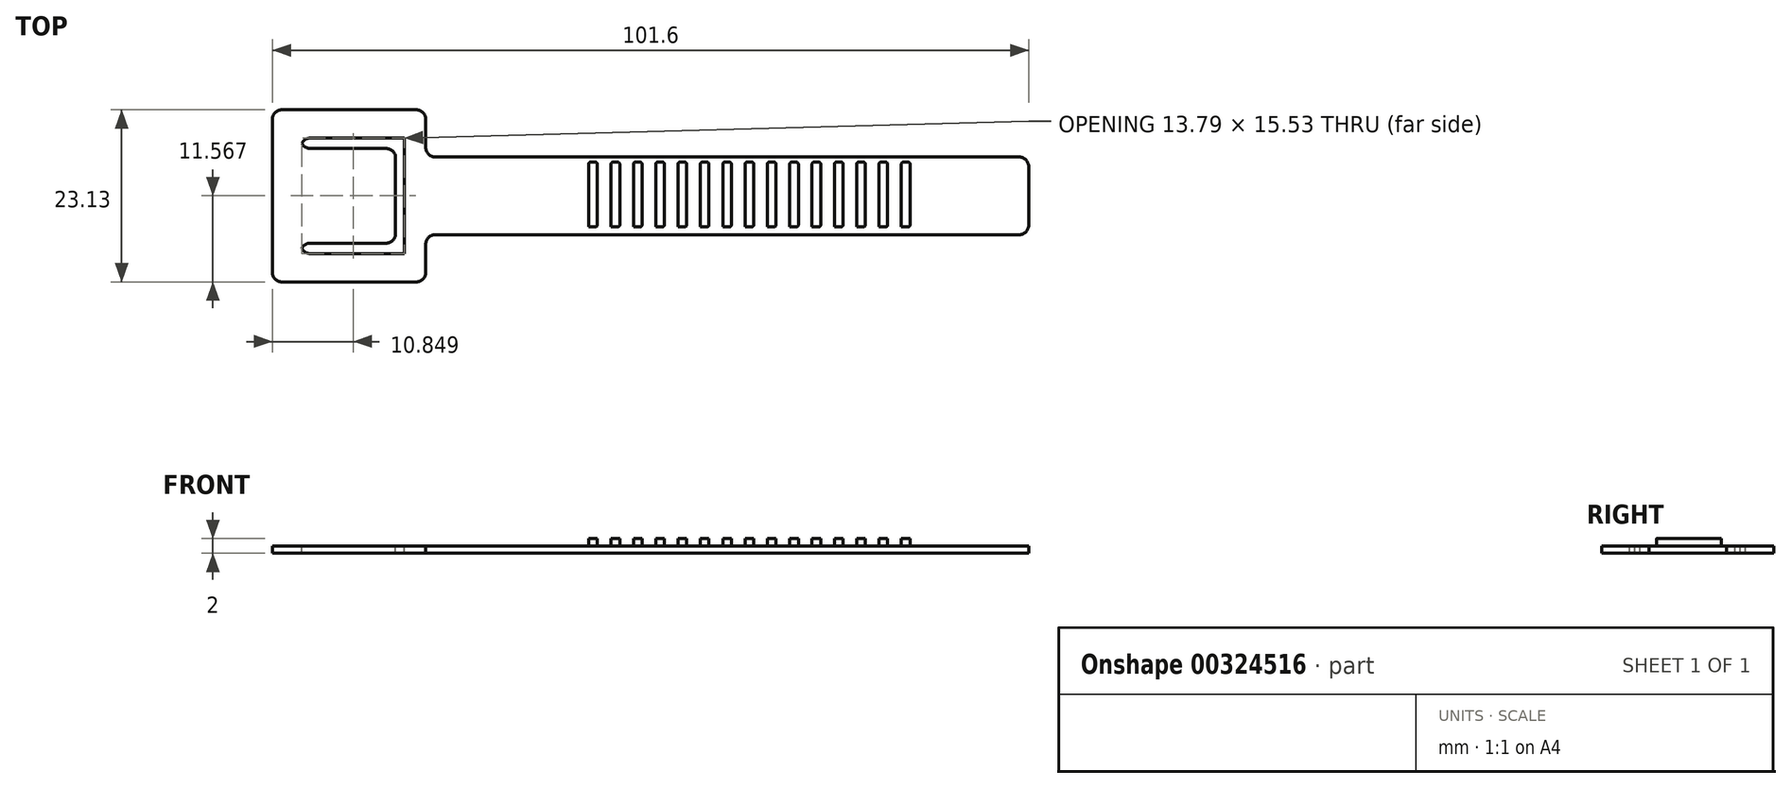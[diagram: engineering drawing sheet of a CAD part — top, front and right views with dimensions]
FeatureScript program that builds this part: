
annotation { "Feature Type Name" : "Feature", "Feature Type Description" : "" }
export const myFeature = defineFeature(function(context is Context, id is Id, definition is map)
    precondition{}
    {
        {
            var Q0;
            Q0=qCreatedBy(makeId("Top.planeOp"),FACE);
            var sketch = newSketch(context, id + "F0", { "sketchPlane" : qUnion([Q0])});
            skLineSegment(sketch, "E0.bottom", {"start": v(-20.62, 27.91) * mm, "end": v(57.84, 27.91) * mm});
            skLineSegment(sketch, "E0.top", {"start": v(-20.62, 17.48) * mm, "end": v(57.84, 17.48) * mm});
            skLineSegment(sketch, "E0.right", {"start": v(59.11, 26.64) * mm, "end": v(59.11, 18.75) * mm});
            skLineSegment(sketch, "E1.bottom", {"start": v(-23.16, 11.13) * mm, "end": v(-41.22, 11.13) * mm});
            skLineSegment(sketch, "E1.top", {"start": v(-23.16, 34.26) * mm, "end": v(-41.22, 34.26) * mm});
            skLineSegment(sketch, "E1.right", {"start": v(-42.49, 12.4) * mm, "end": v(-42.49, 33) * mm});
            skLineSegment(sketch, "E2", {"start": v(-21.9, 29.18) * mm, "end": v(-21.9, 33) * mm});
            skLineSegment(sketch, "E3", {"start": v(-21.9, 12.4) * mm, "end": v(-21.9, 16.21) * mm});
            skLineSegment(sketch, "E4.bottom", {"start": v(-38.17, 30.7) * mm, "end": v(-25.52, 30.7) * mm});
            skLineSegment(sketch, "E4.top", {"start": v(-38.17, 14.7) * mm, "end": v(-25.52, 14.7) * mm});
            skLineSegment(sketch, "E4.right", {"start": v(-25.52, 30.7) * mm, "end": v(-25.52, 14.7) * mm});
            skLineSegment(sketch, "E5", {"start": v(-39.44, 30.57) * mm, "end": v(-39.44, 29.43) * mm});
            skLineSegment(sketch, "E6", {"start": v(-38.17, 29.3) * mm, "end": v(-27.99, 29.3) * mm});
            skLineSegment(sketch, "E7", {"start": v(-26.72, 28.03) * mm, "end": v(-26.72, 17.36) * mm});
            skLineSegment(sketch, "E8", {"start": v(-27.99, 16.1) * mm, "end": v(-38.17, 16.1) * mm});
            skLineSegment(sketch, "E9", {"start": v(-39.44, 15.96) * mm, "end": v(-39.44, 14.82) * mm});
            skPoint(sketch, "E10.visualSharp", {"position": v(-26.72, 29.3) * mm});
            skArc(sketch, "E10.filletArc", {"start": v(-26.72, 28.03) * mm, "mid": v(-27.09, 28.93) * mm, "end": v(-27.99, 29.3) * mm});
            skPoint(sketch, "E11.visualSharp", {"position": v(-26.72, 16.1) * mm});
            skArc(sketch, "E11.filletArc", {"start": v(-27.99, 16.1) * mm, "mid": v(-27.09, 16.47) * mm, "end": v(-26.72, 17.36) * mm});
            skPoint(sketch, "E12.visualSharp", {"position": v(-39.44, 29.3) * mm});
            skArc(sketch, "E12.filletArc", {"start": v(-39.44, 30.57) * mm, "mid": v(-39.07, 29.67) * mm, "end": v(-38.17, 29.3) * mm});
            skPoint(sketch, "E13.visualSharp", {"position": v(-39.44, 30.7) * mm});
            skArc(sketch, "E13.filletArc", {"start": v(-38.17, 30.7) * mm, "mid": v(-39.07, 30.33) * mm, "end": v(-39.44, 29.43) * mm});
            skPoint(sketch, "E14.visualSharp", {"position": v(-39.44, 16.1) * mm});
            skArc(sketch, "E14.filletArc", {"start": v(-38.17, 16.1) * mm, "mid": v(-39.07, 15.72) * mm, "end": v(-39.44, 14.82) * mm});
            skPoint(sketch, "E15.visualSharp", {"position": v(-39.44, 14.7) * mm});
            skArc(sketch, "E15.filletArc", {"start": v(-39.44, 15.96) * mm, "mid": v(-39.07, 15.07) * mm, "end": v(-38.17, 14.7) * mm});
            skPoint(sketch, "E16.visualSharp", {"position": v(-21.9, 27.91) * mm});
            skArc(sketch, "E16.filletArc", {"start": v(-21.9, 29.18) * mm, "mid": v(-21.52, 28.29) * mm, "end": v(-20.62, 27.91) * mm});
            skPoint(sketch, "E17.visualSharp", {"position": v(-21.9, 17.48) * mm});
            skArc(sketch, "E17.filletArc", {"start": v(-20.62, 17.48) * mm, "mid": v(-21.52, 17.1) * mm, "end": v(-21.9, 16.21) * mm});
            skPoint(sketch, "E18.visualSharp", {"position": v(-21.9, 11.13) * mm});
            skArc(sketch, "E18.filletArc", {"start": v(-23.16, 11.13) * mm, "mid": v(-22.26, 11.5) * mm, "end": v(-21.9, 12.4) * mm});
            skPoint(sketch, "E19.visualSharp", {"position": v(-42.49, 11.13) * mm});
            skArc(sketch, "E19.filletArc", {"start": v(-42.49, 12.4) * mm, "mid": v(-42.12, 11.5) * mm, "end": v(-41.22, 11.13) * mm});
            skPoint(sketch, "E20.visualSharp", {"position": v(-42.49, 34.26) * mm});
            skArc(sketch, "E20.filletArc", {"start": v(-41.22, 34.26) * mm, "mid": v(-42.12, 33.9) * mm, "end": v(-42.49, 33) * mm});
            skPoint(sketch, "E21.visualSharp", {"position": v(-21.9, 34.26) * mm});
            skArc(sketch, "E21.filletArc", {"start": v(-21.9, 33) * mm, "mid": v(-22.26, 33.9) * mm, "end": v(-23.16, 34.26) * mm});
            skPoint(sketch, "E22.visualSharp", {"position": v(59.11, 27.91) * mm});
            skArc(sketch, "E22.filletArc", {"start": v(59.11, 26.64) * mm, "mid": v(58.74, 27.54) * mm, "end": v(57.84, 27.91) * mm});
            skPoint(sketch, "E23.visualSharp", {"position": v(59.11, 17.48) * mm});
            skArc(sketch, "E23.filletArc", {"start": v(57.84, 17.48) * mm, "mid": v(58.74, 17.85) * mm, "end": v(59.11, 18.75) * mm});
            skSolve(sketch);
        }
        {
            var Q0;
            Q0=makeQuery(id+"F0.imprint","IMPRINT",FACE,{"disambiguationData":[TD([[makeQuery(id+"F0.imprint","IMPRINT",EDGE,{"derivedFrom":sQuery(id+"F0.wireOp",EDGE,"E0.bottom")}),-1.0]])]});
            var Q1;
            {var subQ5=sQuery(id+"F0.wireOp",EDGE,"E4.bottom");Q1=makeQuery(id+"F0.imprint","IMPRINT",FACE,{"disambiguationData":[TD([[makeQuery(id+"F0.imprint","IMPRINT",EDGE,{"derivedFrom":subQ5}),-1.0]])]});}
            var Q2;
            {var subQ0=sQuery(id+"F0.wireOp",EDGE,"E5");Q2=makeQuery(id+"F0.imprint","IMPRINT",FACE,{"disambiguationData":[TD([[makeQuery(id+"F0.imprint","IMPRINT",EDGE,{"derivedFrom":subQ0}),1.0]])]});}
            var Q3;
            {var subQ0=sQuery(id+"F0.wireOp",EDGE,"E9");Q3=makeQuery(id+"F0.imprint","IMPRINT",FACE,{"disambiguationData":[TD([[makeQuery(id+"F0.imprint","IMPRINT",EDGE,{"derivedFrom":subQ0}),1.0]])]});}
            extrude(context, id + "F1", {"entities" : qUnion([Q0, Q1, Q2, Q3]), "depth" : 1 * mm});
        }
        {
            var Q0;
            Q0=makeQuery(id+"F1.opExtrude","CAP_FACE",FACE,{"disambiguationData":[OSD([sQuery(id+"F0.wireOp",EDGE,"E0.bottom"),sQuery(id+"F0.wireOp",EDGE,"E0.top"),sQuery(id+"F0.wireOp",EDGE,"E0.right"),sQuery(id+"F0.wireOp",EDGE,"E1.bottom"),sQuery(id+"F0.wireOp",EDGE,"E1.top"),sQuery(id+"F0.wireOp",EDGE,"E1.right"),sQuery(id+"F0.wireOp",EDGE,"E2"),sQuery(id+"F0.wireOp",EDGE,"E3"),sQuery(id+"F0.wireOp",EDGE,"E16.filletArc"),sQuery(id+"F0.wireOp",EDGE,"E17.filletArc"),sQuery(id+"F0.wireOp",EDGE,"E18.filletArc"),sQuery(id+"F0.wireOp",EDGE,"E19.filletArc"),sQuery(id+"F0.wireOp",EDGE,"E20.filletArc"),sQuery(id+"F0.wireOp",EDGE,"E21.filletArc"),sQuery(id+"F0.wireOp",EDGE,"E22.filletArc"),sQuery(id+"F0.wireOp",EDGE,"E23.filletArc")])],"isStart":false});
            var sketch = newSketch(context, id + "F2", { "sketchPlane" : qUnion([Q0])});
            skLineSegment(sketch, "E24.bottom", {"start": v(-37.4, 30.46) * mm, "end": v(-24.74, 30.46) * mm});
            skLineSegment(sketch, "E24.top", {"start": v(-37.4, 14.93) * mm, "end": v(-24.74, 14.93) * mm});
            skLineSegment(sketch, "E24.right", {"start": v(-24.74, 30.46) * mm, "end": v(-24.74, 14.93) * mm});
            skLineSegment(sketch, "E25", {"start": v(-37.4, 29.06) * mm, "end": v(-27.21, 29.06) * mm});
            skLineSegment(sketch, "E26", {"start": v(-25.94, 27.8) * mm, "end": v(-25.94, 17.6) * mm});
            skLineSegment(sketch, "E27", {"start": v(-27.21, 16.33) * mm, "end": v(-37.4, 16.33) * mm});
            skPoint(sketch, "E28.visualSharp", {"position": v(-25.94, 29.06) * mm});
            skArc(sketch, "E28.filletArc", {"start": v(-25.94, 27.8) * mm, "mid": v(-26.32, 28.7) * mm, "end": v(-27.21, 29.06) * mm});
            skPoint(sketch, "E29.visualSharp", {"position": v(-25.94, 16.33) * mm});
            skArc(sketch, "E29.filletArc", {"start": v(-27.21, 16.33) * mm, "mid": v(-26.32, 16.7) * mm, "end": v(-25.94, 17.6) * mm});
            skPoint(sketch, "E30.visualSharp", {"position": v(-38.67, 29.06) * mm});
            skArc(sketch, "E30.filletArc", {"start": v(-38.67, 30.33) * mm, "mid": v(-38.3, 29.43) * mm, "end": v(-37.4, 29.06) * mm});
            skPoint(sketch, "E31.visualSharp", {"position": v(-38.67, 30.46) * mm});
            skArc(sketch, "E31.filletArc", {"start": v(-37.4, 30.46) * mm, "mid": v(-38.3, 30.1) * mm, "end": v(-38.67, 29.2) * mm});
            skPoint(sketch, "E32.visualSharp", {"position": v(-38.67, 16.33) * mm});
            skArc(sketch, "E32.filletArc", {"start": v(-37.4, 16.33) * mm, "mid": v(-38.3, 15.96) * mm, "end": v(-38.67, 15.06) * mm});
            skPoint(sketch, "E33.visualSharp", {"position": v(-38.67, 14.93) * mm});
            skArc(sketch, "E33.filletArc", {"start": v(-38.67, 16.2) * mm, "mid": v(-38.3, 15.3) * mm, "end": v(-37.4, 14.93) * mm});
            skLineSegment(sketch, "E34", {"start": v(-32.3, 30.46) * mm, "end": v(-32.3, 34.26) * mm});
            skLineSegment(sketch, "E35", {"start": v(-32.19, 11.13) * mm, "end": v(-32.19, 14.93) * mm});
            skSolve(sketch);
        }
        {
            var Q0;
            Q0 = qSketchRegion(id + "F2", true);
            extrude(context, id + "F3", {"entities" : qUnion([Q0]), "operationType" : NewBodyOperationType.REMOVE, "oppositeDirection" : true, "depth" : 25.4 * mm});
        }
        {
            var Q0;
            Q0=makeQuery(id+"F1.opExtrude","CAP_FACE",FACE,{"disambiguationData":[OSD([sQuery(id+"F0.wireOp",EDGE,"E0.bottom"),sQuery(id+"F0.wireOp",EDGE,"E0.top"),sQuery(id+"F0.wireOp",EDGE,"E0.right"),sQuery(id+"F0.wireOp",EDGE,"E1.bottom"),sQuery(id+"F0.wireOp",EDGE,"E1.top"),sQuery(id+"F0.wireOp",EDGE,"E1.right"),sQuery(id+"F0.wireOp",EDGE,"E2"),sQuery(id+"F0.wireOp",EDGE,"E3"),sQuery(id+"F0.wireOp",EDGE,"E16.filletArc"),sQuery(id+"F0.wireOp",EDGE,"E17.filletArc"),sQuery(id+"F0.wireOp",EDGE,"E18.filletArc"),sQuery(id+"F0.wireOp",EDGE,"E19.filletArc"),sQuery(id+"F0.wireOp",EDGE,"E20.filletArc"),sQuery(id+"F0.wireOp",EDGE,"E21.filletArc"),sQuery(id+"F0.wireOp",EDGE,"E22.filletArc"),sQuery(id+"F0.wireOp",EDGE,"E23.filletArc")])],"isStart":false});
            var sketch = newSketch(context, id + "F4", { "sketchPlane" : qUnion([Q0])});
            skLineSegment(sketch, "E36.bottom", {"start": v(0.25, 27.22) * mm, "end": v(0.9, 27.22) * mm});
            skLineSegment(sketch, "E36.left", {"start": v(0, 26.97) * mm, "end": v(0, 18.42) * mm});
            skArc(sketch, "E37.filletArc", {"start": v(1.16, 26.97) * mm, "mid": v(1.09, 27.15) * mm, "end": v(0.9, 27.22) * mm});
            skPoint(sketch, "E38.visualSharp", {"position": v(0, 27.22) * mm});
            skArc(sketch, "E38.filletArc", {"start": v(0.25, 27.22) * mm, "mid": v(0.07, 27.15) * mm, "end": v(0, 26.97) * mm});
            skPoint(sketch, "E39.visualSharp", {"position": v(0, 18.51) * mm});
            skArc(sketch, "E39.filletArc", {"start": v(0, 18.42) * mm, "mid": v(-0.15, 18.36) * mm, "end": v(-0.09, 18.51) * mm});
            skLineSegment(sketch, "E40", {"start": v(1.16, 26.97) * mm, "end": v(1.16, 18.78) * mm});
            skLineSegment(sketch, "E41", {"start": v(0.91, 18.53) * mm, "end": v(0, 18.51) * mm});
            skPoint(sketch, "E42.visualSharp", {"position": v(1.16, 18.53) * mm});
            skArc(sketch, "E42.filletArc", {"start": v(0.91, 18.53) * mm, "mid": v(1.09, 18.6) * mm, "end": v(1.16, 18.78) * mm});
            skPoint(sketch, "E43.1.0.0", {"position": v(4.16, 18.53) * mm});
            skPoint(sketch, "E43.1.0.1", {"position": v(3, 18.51) * mm});
            skLineSegment(sketch, "E43.1.0.2", {"start": v(3.25, 27.22) * mm, "end": v(3.9, 27.22) * mm});
            skLineSegment(sketch, "E43.1.0.3", {"start": v(3, 26.97) * mm, "end": v(3, 18.42) * mm});
            skPoint(sketch, "E43.1.0.4", {"position": v(3, 27.22) * mm});
            skLineSegment(sketch, "E43.1.0.5", {"start": v(4.16, 26.97) * mm, "end": v(4.16, 18.78) * mm});
            skLineSegment(sketch, "E43.1.0.6", {"start": v(3.91, 18.53) * mm, "end": v(3, 18.51) * mm});
            skArc(sketch, "E43.1.0.7", {"start": v(4.16, 26.97) * mm, "mid": v(4.09, 27.15) * mm, "end": v(3.9, 27.22) * mm});
            skArc(sketch, "E43.1.0.8", {"start": v(3.25, 27.22) * mm, "mid": v(3.07, 27.15) * mm, "end": v(3, 26.97) * mm});
            skArc(sketch, "E43.1.0.9", {"start": v(3, 18.42) * mm, "mid": v(2.85, 18.36) * mm, "end": v(2.91, 18.51) * mm});
            skArc(sketch, "E43.1.0.10", {"start": v(3.91, 18.53) * mm, "mid": v(4.09, 18.6) * mm, "end": v(4.16, 18.78) * mm});
            skPoint(sketch, "E43.2.0.0", {"position": v(7.16, 18.53) * mm});
            skPoint(sketch, "E43.2.0.1", {"position": v(6, 18.51) * mm});
            skLineSegment(sketch, "E43.2.0.2", {"start": v(6.25, 27.22) * mm, "end": v(6.9, 27.22) * mm});
            skLineSegment(sketch, "E43.2.0.3", {"start": v(6, 26.97) * mm, "end": v(6, 18.42) * mm});
            skPoint(sketch, "E43.2.0.4", {"position": v(6, 27.22) * mm});
            skLineSegment(sketch, "E43.2.0.5", {"start": v(7.16, 26.97) * mm, "end": v(7.16, 18.78) * mm});
            skLineSegment(sketch, "E43.2.0.6", {"start": v(6.91, 18.53) * mm, "end": v(6, 18.51) * mm});
            skArc(sketch, "E43.2.0.7", {"start": v(7.16, 26.97) * mm, "mid": v(7.09, 27.15) * mm, "end": v(6.9, 27.22) * mm});
            skArc(sketch, "E43.2.0.8", {"start": v(6.25, 27.22) * mm, "mid": v(6.07, 27.15) * mm, "end": v(6, 26.97) * mm});
            skArc(sketch, "E43.2.0.9", {"start": v(6, 18.42) * mm, "mid": v(5.85, 18.36) * mm, "end": v(5.91, 18.51) * mm});
            skArc(sketch, "E43.2.0.10", {"start": v(6.91, 18.53) * mm, "mid": v(7.09, 18.6) * mm, "end": v(7.16, 18.78) * mm});
            skPoint(sketch, "E43.3.0.0", {"position": v(10.16, 18.53) * mm});
            skPoint(sketch, "E43.3.0.1", {"position": v(9, 18.51) * mm});
            skLineSegment(sketch, "E43.3.0.2", {"start": v(9.25, 27.22) * mm, "end": v(9.9, 27.22) * mm});
            skLineSegment(sketch, "E43.3.0.3", {"start": v(9, 26.97) * mm, "end": v(9, 18.42) * mm});
            skPoint(sketch, "E43.3.0.4", {"position": v(9, 27.22) * mm});
            skLineSegment(sketch, "E43.3.0.5", {"start": v(10.16, 26.97) * mm, "end": v(10.16, 18.78) * mm});
            skLineSegment(sketch, "E43.3.0.6", {"start": v(9.91, 18.53) * mm, "end": v(9, 18.51) * mm});
            skArc(sketch, "E43.3.0.7", {"start": v(10.16, 26.97) * mm, "mid": v(10.09, 27.15) * mm, "end": v(9.9, 27.22) * mm});
            skArc(sketch, "E43.3.0.8", {"start": v(9.25, 27.22) * mm, "mid": v(9.07, 27.15) * mm, "end": v(9, 26.97) * mm});
            skArc(sketch, "E43.3.0.9", {"start": v(9, 18.42) * mm, "mid": v(8.85, 18.36) * mm, "end": v(8.91, 18.51) * mm});
            skArc(sketch, "E43.3.0.10", {"start": v(9.91, 18.53) * mm, "mid": v(10.09, 18.6) * mm, "end": v(10.16, 18.78) * mm});
            skPoint(sketch, "E43.4.0.0", {"position": v(13.16, 18.53) * mm});
            skPoint(sketch, "E43.4.0.1", {"position": v(12, 18.51) * mm});
            skLineSegment(sketch, "E43.4.0.2", {"start": v(12.25, 27.22) * mm, "end": v(12.9, 27.22) * mm});
            skLineSegment(sketch, "E43.4.0.3", {"start": v(12, 26.97) * mm, "end": v(12, 18.42) * mm});
            skPoint(sketch, "E43.4.0.4", {"position": v(12, 27.22) * mm});
            skLineSegment(sketch, "E43.4.0.5", {"start": v(13.16, 26.97) * mm, "end": v(13.16, 18.78) * mm});
            skLineSegment(sketch, "E43.4.0.6", {"start": v(12.91, 18.53) * mm, "end": v(12, 18.51) * mm});
            skArc(sketch, "E43.4.0.7", {"start": v(13.16, 26.97) * mm, "mid": v(13.09, 27.15) * mm, "end": v(12.9, 27.22) * mm});
            skArc(sketch, "E43.4.0.8", {"start": v(12.25, 27.22) * mm, "mid": v(12.07, 27.15) * mm, "end": v(12, 26.97) * mm});
            skArc(sketch, "E43.4.0.9", {"start": v(12, 18.42) * mm, "mid": v(11.85, 18.36) * mm, "end": v(11.91, 18.51) * mm});
            skArc(sketch, "E43.4.0.10", {"start": v(12.91, 18.53) * mm, "mid": v(13.09, 18.6) * mm, "end": v(13.16, 18.78) * mm});
            skPoint(sketch, "E43.5.0.0", {"position": v(16.16, 18.53) * mm});
            skPoint(sketch, "E43.5.0.1", {"position": v(15, 18.51) * mm});
            skLineSegment(sketch, "E43.5.0.2", {"start": v(15.25, 27.22) * mm, "end": v(15.9, 27.22) * mm});
            skLineSegment(sketch, "E43.5.0.3", {"start": v(15, 26.97) * mm, "end": v(15, 18.42) * mm});
            skPoint(sketch, "E43.5.0.4", {"position": v(15, 27.22) * mm});
            skLineSegment(sketch, "E43.5.0.5", {"start": v(16.16, 26.97) * mm, "end": v(16.16, 18.78) * mm});
            skLineSegment(sketch, "E43.5.0.6", {"start": v(15.91, 18.53) * mm, "end": v(15, 18.51) * mm});
            skArc(sketch, "E43.5.0.7", {"start": v(16.16, 26.97) * mm, "mid": v(16.09, 27.15) * mm, "end": v(15.9, 27.22) * mm});
            skArc(sketch, "E43.5.0.8", {"start": v(15.25, 27.22) * mm, "mid": v(15.07, 27.15) * mm, "end": v(15, 26.97) * mm});
            skArc(sketch, "E43.5.0.9", {"start": v(15, 18.42) * mm, "mid": v(14.85, 18.36) * mm, "end": v(14.91, 18.51) * mm});
            skArc(sketch, "E43.5.0.10", {"start": v(15.91, 18.53) * mm, "mid": v(16.09, 18.6) * mm, "end": v(16.16, 18.78) * mm});
            skPoint(sketch, "E43.6.0.0", {"position": v(19.16, 18.53) * mm});
            skPoint(sketch, "E43.6.0.1", {"position": v(18, 18.51) * mm});
            skLineSegment(sketch, "E43.6.0.2", {"start": v(18.25, 27.22) * mm, "end": v(18.9, 27.22) * mm});
            skLineSegment(sketch, "E43.6.0.3", {"start": v(18, 26.97) * mm, "end": v(18, 18.42) * mm});
            skPoint(sketch, "E43.6.0.4", {"position": v(18, 27.22) * mm});
            skLineSegment(sketch, "E43.6.0.5", {"start": v(19.16, 26.97) * mm, "end": v(19.16, 18.78) * mm});
            skLineSegment(sketch, "E43.6.0.6", {"start": v(18.91, 18.53) * mm, "end": v(18, 18.51) * mm});
            skArc(sketch, "E43.6.0.7", {"start": v(19.16, 26.97) * mm, "mid": v(19.09, 27.15) * mm, "end": v(18.9, 27.22) * mm});
            skArc(sketch, "E43.6.0.8", {"start": v(18.25, 27.22) * mm, "mid": v(18.07, 27.15) * mm, "end": v(18, 26.97) * mm});
            skArc(sketch, "E43.6.0.9", {"start": v(18, 18.42) * mm, "mid": v(17.85, 18.36) * mm, "end": v(17.91, 18.51) * mm});
            skArc(sketch, "E43.6.0.10", {"start": v(18.91, 18.53) * mm, "mid": v(19.09, 18.6) * mm, "end": v(19.16, 18.78) * mm});
            skPoint(sketch, "E43.7.0.0", {"position": v(22.16, 18.53) * mm});
            skPoint(sketch, "E43.7.0.1", {"position": v(21, 18.51) * mm});
            skLineSegment(sketch, "E43.7.0.2", {"start": v(21.25, 27.22) * mm, "end": v(21.9, 27.22) * mm});
            skLineSegment(sketch, "E43.7.0.3", {"start": v(21, 26.97) * mm, "end": v(21, 18.42) * mm});
            skPoint(sketch, "E43.7.0.4", {"position": v(21, 27.22) * mm});
            skLineSegment(sketch, "E43.7.0.5", {"start": v(22.16, 26.97) * mm, "end": v(22.16, 18.78) * mm});
            skLineSegment(sketch, "E43.7.0.6", {"start": v(21.91, 18.53) * mm, "end": v(21, 18.51) * mm});
            skArc(sketch, "E43.7.0.7", {"start": v(22.16, 26.97) * mm, "mid": v(22.09, 27.15) * mm, "end": v(21.9, 27.22) * mm});
            skArc(sketch, "E43.7.0.8", {"start": v(21.25, 27.22) * mm, "mid": v(21.07, 27.15) * mm, "end": v(21, 26.97) * mm});
            skArc(sketch, "E43.7.0.9", {"start": v(21, 18.42) * mm, "mid": v(20.85, 18.36) * mm, "end": v(20.91, 18.51) * mm});
            skArc(sketch, "E43.7.0.10", {"start": v(21.91, 18.53) * mm, "mid": v(22.09, 18.6) * mm, "end": v(22.16, 18.78) * mm});
            skPoint(sketch, "E43.8.0.0", {"position": v(25.16, 18.53) * mm});
            skPoint(sketch, "E43.8.0.1", {"position": v(24, 18.51) * mm});
            skLineSegment(sketch, "E43.8.0.2", {"start": v(24.25, 27.22) * mm, "end": v(24.9, 27.22) * mm});
            skLineSegment(sketch, "E43.8.0.3", {"start": v(24, 26.97) * mm, "end": v(24, 18.42) * mm});
            skPoint(sketch, "E43.8.0.4", {"position": v(24, 27.22) * mm});
            skLineSegment(sketch, "E43.8.0.5", {"start": v(25.16, 26.97) * mm, "end": v(25.16, 18.78) * mm});
            skLineSegment(sketch, "E43.8.0.6", {"start": v(24.91, 18.53) * mm, "end": v(24, 18.51) * mm});
            skArc(sketch, "E43.8.0.7", {"start": v(25.16, 26.97) * mm, "mid": v(25.09, 27.15) * mm, "end": v(24.9, 27.22) * mm});
            skArc(sketch, "E43.8.0.8", {"start": v(24.25, 27.22) * mm, "mid": v(24.07, 27.15) * mm, "end": v(24, 26.97) * mm});
            skArc(sketch, "E43.8.0.9", {"start": v(24, 18.42) * mm, "mid": v(23.85, 18.36) * mm, "end": v(23.91, 18.51) * mm});
            skArc(sketch, "E43.8.0.10", {"start": v(24.91, 18.53) * mm, "mid": v(25.09, 18.6) * mm, "end": v(25.16, 18.78) * mm});
            skPoint(sketch, "E43.9.0.0", {"position": v(28.16, 18.53) * mm});
            skPoint(sketch, "E43.9.0.1", {"position": v(27, 18.51) * mm});
            skLineSegment(sketch, "E43.9.0.2", {"start": v(27.25, 27.22) * mm, "end": v(27.9, 27.22) * mm});
            skLineSegment(sketch, "E43.9.0.3", {"start": v(27, 26.97) * mm, "end": v(27, 18.42) * mm});
            skPoint(sketch, "E43.9.0.4", {"position": v(27, 27.22) * mm});
            skLineSegment(sketch, "E43.9.0.5", {"start": v(28.16, 26.97) * mm, "end": v(28.16, 18.78) * mm});
            skLineSegment(sketch, "E43.9.0.6", {"start": v(27.91, 18.53) * mm, "end": v(27, 18.51) * mm});
            skArc(sketch, "E43.9.0.7", {"start": v(28.16, 26.97) * mm, "mid": v(28.09, 27.15) * mm, "end": v(27.9, 27.22) * mm});
            skArc(sketch, "E43.9.0.8", {"start": v(27.25, 27.22) * mm, "mid": v(27.07, 27.15) * mm, "end": v(27, 26.97) * mm});
            skArc(sketch, "E43.9.0.9", {"start": v(27, 18.42) * mm, "mid": v(26.85, 18.36) * mm, "end": v(26.91, 18.51) * mm});
            skArc(sketch, "E43.9.0.10", {"start": v(27.91, 18.53) * mm, "mid": v(28.09, 18.6) * mm, "end": v(28.16, 18.78) * mm});
            skPoint(sketch, "E43.10.0.0", {"position": v(31.16, 18.53) * mm});
            skPoint(sketch, "E43.10.0.1", {"position": v(30, 18.51) * mm});
            skLineSegment(sketch, "E43.10.0.2", {"start": v(30.25, 27.22) * mm, "end": v(30.9, 27.22) * mm});
            skLineSegment(sketch, "E43.10.0.3", {"start": v(30, 26.97) * mm, "end": v(30, 18.42) * mm});
            skPoint(sketch, "E43.10.0.4", {"position": v(30, 27.22) * mm});
            skLineSegment(sketch, "E43.10.0.5", {"start": v(31.16, 26.97) * mm, "end": v(31.16, 18.78) * mm});
            skLineSegment(sketch, "E43.10.0.6", {"start": v(30.91, 18.53) * mm, "end": v(30, 18.51) * mm});
            skArc(sketch, "E43.10.0.7", {"start": v(31.16, 26.97) * mm, "mid": v(31.09, 27.15) * mm, "end": v(30.9, 27.22) * mm});
            skArc(sketch, "E43.10.0.8", {"start": v(30.25, 27.22) * mm, "mid": v(30.07, 27.15) * mm, "end": v(30, 26.97) * mm});
            skArc(sketch, "E43.10.0.9", {"start": v(30, 18.42) * mm, "mid": v(29.85, 18.36) * mm, "end": v(29.91, 18.51) * mm});
            skArc(sketch, "E43.10.0.10", {"start": v(30.91, 18.53) * mm, "mid": v(31.09, 18.6) * mm, "end": v(31.16, 18.78) * mm});
            skPoint(sketch, "E43.11.0.0", {"position": v(34.16, 18.53) * mm});
            skPoint(sketch, "E43.11.0.1", {"position": v(33, 18.51) * mm});
            skLineSegment(sketch, "E43.11.0.2", {"start": v(33.25, 27.22) * mm, "end": v(33.9, 27.22) * mm});
            skLineSegment(sketch, "E43.11.0.3", {"start": v(33, 26.97) * mm, "end": v(33, 18.42) * mm});
            skPoint(sketch, "E43.11.0.4", {"position": v(33, 27.22) * mm});
            skLineSegment(sketch, "E43.11.0.5", {"start": v(34.16, 26.97) * mm, "end": v(34.16, 18.78) * mm});
            skLineSegment(sketch, "E43.11.0.6", {"start": v(33.91, 18.53) * mm, "end": v(33, 18.51) * mm});
            skArc(sketch, "E43.11.0.7", {"start": v(34.16, 26.97) * mm, "mid": v(34.09, 27.15) * mm, "end": v(33.9, 27.22) * mm});
            skArc(sketch, "E43.11.0.8", {"start": v(33.25, 27.22) * mm, "mid": v(33.07, 27.15) * mm, "end": v(33, 26.97) * mm});
            skArc(sketch, "E43.11.0.9", {"start": v(33, 18.42) * mm, "mid": v(32.85, 18.36) * mm, "end": v(32.91, 18.51) * mm});
            skArc(sketch, "E43.11.0.10", {"start": v(33.91, 18.53) * mm, "mid": v(34.09, 18.6) * mm, "end": v(34.16, 18.78) * mm});
            skPoint(sketch, "E43.12.0.0", {"position": v(37.16, 18.53) * mm});
            skPoint(sketch, "E43.12.0.1", {"position": v(36, 18.51) * mm});
            skLineSegment(sketch, "E43.12.0.2", {"start": v(36.25, 27.22) * mm, "end": v(36.9, 27.22) * mm});
            skLineSegment(sketch, "E43.12.0.3", {"start": v(36, 26.97) * mm, "end": v(36, 18.42) * mm});
            skPoint(sketch, "E43.12.0.4", {"position": v(36, 27.22) * mm});
            skLineSegment(sketch, "E43.12.0.5", {"start": v(37.16, 26.97) * mm, "end": v(37.16, 18.78) * mm});
            skLineSegment(sketch, "E43.12.0.6", {"start": v(36.91, 18.53) * mm, "end": v(36, 18.51) * mm});
            skArc(sketch, "E43.12.0.7", {"start": v(37.16, 26.97) * mm, "mid": v(37.09, 27.15) * mm, "end": v(36.9, 27.22) * mm});
            skArc(sketch, "E43.12.0.8", {"start": v(36.25, 27.22) * mm, "mid": v(36.07, 27.15) * mm, "end": v(36, 26.97) * mm});
            skArc(sketch, "E43.12.0.9", {"start": v(36, 18.42) * mm, "mid": v(35.85, 18.36) * mm, "end": v(35.91, 18.51) * mm});
            skArc(sketch, "E43.12.0.10", {"start": v(36.91, 18.53) * mm, "mid": v(37.09, 18.6) * mm, "end": v(37.16, 18.78) * mm});
            skPoint(sketch, "E43.13.0.0", {"position": v(40.16, 18.53) * mm});
            skPoint(sketch, "E43.13.0.1", {"position": v(39, 18.51) * mm});
            skLineSegment(sketch, "E43.13.0.2", {"start": v(39.25, 27.22) * mm, "end": v(39.9, 27.22) * mm});
            skLineSegment(sketch, "E43.13.0.3", {"start": v(39, 26.97) * mm, "end": v(39, 18.42) * mm});
            skPoint(sketch, "E43.13.0.4", {"position": v(39, 27.22) * mm});
            skLineSegment(sketch, "E43.13.0.5", {"start": v(40.16, 26.97) * mm, "end": v(40.16, 18.78) * mm});
            skLineSegment(sketch, "E43.13.0.6", {"start": v(39.91, 18.53) * mm, "end": v(39, 18.51) * mm});
            skArc(sketch, "E43.13.0.7", {"start": v(40.16, 26.97) * mm, "mid": v(40.09, 27.15) * mm, "end": v(39.9, 27.22) * mm});
            skArc(sketch, "E43.13.0.8", {"start": v(39.25, 27.22) * mm, "mid": v(39.07, 27.15) * mm, "end": v(39, 26.97) * mm});
            skArc(sketch, "E43.13.0.9", {"start": v(39, 18.42) * mm, "mid": v(38.85, 18.36) * mm, "end": v(38.91, 18.51) * mm});
            skArc(sketch, "E43.13.0.10", {"start": v(39.91, 18.53) * mm, "mid": v(40.09, 18.6) * mm, "end": v(40.16, 18.78) * mm});
            skPoint(sketch, "E43.14.0.0", {"position": v(43.16, 18.53) * mm});
            skPoint(sketch, "E43.14.0.1", {"position": v(42, 18.51) * mm});
            skLineSegment(sketch, "E43.14.0.2", {"start": v(42.25, 27.22) * mm, "end": v(42.9, 27.22) * mm});
            skLineSegment(sketch, "E43.14.0.3", {"start": v(42, 26.97) * mm, "end": v(42, 18.42) * mm});
            skPoint(sketch, "E43.14.0.4", {"position": v(42, 27.22) * mm});
            skLineSegment(sketch, "E43.14.0.5", {"start": v(43.16, 26.97) * mm, "end": v(43.16, 18.78) * mm});
            skLineSegment(sketch, "E43.14.0.6", {"start": v(42.91, 18.53) * mm, "end": v(42, 18.51) * mm});
            skArc(sketch, "E43.14.0.7", {"start": v(43.16, 26.97) * mm, "mid": v(43.09, 27.15) * mm, "end": v(42.9, 27.22) * mm});
            skArc(sketch, "E43.14.0.8", {"start": v(42.25, 27.22) * mm, "mid": v(42.07, 27.15) * mm, "end": v(42, 26.97) * mm});
            skArc(sketch, "E43.14.0.9", {"start": v(42, 18.42) * mm, "mid": v(41.85, 18.36) * mm, "end": v(41.91, 18.51) * mm});
            skArc(sketch, "E43.14.0.10", {"start": v(42.91, 18.53) * mm, "mid": v(43.09, 18.6) * mm, "end": v(43.16, 18.78) * mm});
            skLineSegment(sketch, "E43.direction1", {"start": v(-0.09, 18.42) * mm, "end": v(2.91, 18.42) * mm, "construction": true});
            skSolve(sketch);
        }
        {
            var Q0;
            Q0=makeQuery(id+"F4.imprint","IMPRINT",FACE,{"disambiguationData":[TD([[makeQuery(id+"F4.imprint","IMPRINT",EDGE,{"derivedFrom":sQuery(id+"F4.wireOp",EDGE,"E36.bottom")}),-1.0]])]});
            var Q1;
            Q1=makeQuery(id+"F4.imprint","IMPRINT",FACE,{"disambiguationData":[TD([[makeQuery(id+"F4.imprint","IMPRINT",EDGE,{"derivedFrom":sQuery(id+"F4.wireOp",EDGE,"E43.1.0.2")}),-1.0]])]});
            var Q2;
            Q2=makeQuery(id+"F4.imprint","IMPRINT",FACE,{"disambiguationData":[TD([[makeQuery(id+"F4.imprint","IMPRINT",EDGE,{"derivedFrom":sQuery(id+"F4.wireOp",EDGE,"E43.2.0.2")}),-1.0]])]});
            var Q3;
            Q3=makeQuery(id+"F4.imprint","IMPRINT",FACE,{"disambiguationData":[TD([[makeQuery(id+"F4.imprint","IMPRINT",EDGE,{"derivedFrom":sQuery(id+"F4.wireOp",EDGE,"E43.3.0.2")}),-1.0]])]});
            var Q4;
            Q4=makeQuery(id+"F4.imprint","IMPRINT",FACE,{"disambiguationData":[TD([[makeQuery(id+"F4.imprint","IMPRINT",EDGE,{"derivedFrom":sQuery(id+"F4.wireOp",EDGE,"E43.4.0.2")}),-1.0]])]});
            var Q5;
            Q5=makeQuery(id+"F4.imprint","IMPRINT",FACE,{"disambiguationData":[TD([[makeQuery(id+"F4.imprint","IMPRINT",EDGE,{"derivedFrom":sQuery(id+"F4.wireOp",EDGE,"E43.5.0.2")}),-1.0]])]});
            var Q6;
            Q6=makeQuery(id+"F4.imprint","IMPRINT",FACE,{"disambiguationData":[TD([[makeQuery(id+"F4.imprint","IMPRINT",EDGE,{"derivedFrom":sQuery(id+"F4.wireOp",EDGE,"E43.6.0.2")}),-1.0]])]});
            var Q7;
            Q7=makeQuery(id+"F4.imprint","IMPRINT",FACE,{"disambiguationData":[TD([[makeQuery(id+"F4.imprint","IMPRINT",EDGE,{"derivedFrom":sQuery(id+"F4.wireOp",EDGE,"E43.14.0.2")}),-1.0]])]});
            var Q8;
            Q8=makeQuery(id+"F4.imprint","IMPRINT",FACE,{"disambiguationData":[TD([[makeQuery(id+"F4.imprint","IMPRINT",EDGE,{"derivedFrom":sQuery(id+"F4.wireOp",EDGE,"E43.13.0.2")}),-1.0]])]});
            var Q9;
            Q9=makeQuery(id+"F4.imprint","IMPRINT",FACE,{"disambiguationData":[TD([[makeQuery(id+"F4.imprint","IMPRINT",EDGE,{"derivedFrom":sQuery(id+"F4.wireOp",EDGE,"E43.12.0.2")}),-1.0]])]});
            var Q10;
            Q10=makeQuery(id+"F4.imprint","IMPRINT",FACE,{"disambiguationData":[TD([[makeQuery(id+"F4.imprint","IMPRINT",EDGE,{"derivedFrom":sQuery(id+"F4.wireOp",EDGE,"E43.11.0.2")}),-1.0]])]});
            var Q11;
            Q11=makeQuery(id+"F4.imprint","IMPRINT",FACE,{"disambiguationData":[TD([[makeQuery(id+"F4.imprint","IMPRINT",EDGE,{"derivedFrom":sQuery(id+"F4.wireOp",EDGE,"E43.10.0.2")}),-1.0]])]});
            var Q12;
            Q12=makeQuery(id+"F4.imprint","IMPRINT",FACE,{"disambiguationData":[TD([[makeQuery(id+"F4.imprint","IMPRINT",EDGE,{"derivedFrom":sQuery(id+"F4.wireOp",EDGE,"E43.9.0.2")}),-1.0]])]});
            var Q13;
            Q13=makeQuery(id+"F4.imprint","IMPRINT",FACE,{"disambiguationData":[TD([[makeQuery(id+"F4.imprint","IMPRINT",EDGE,{"derivedFrom":sQuery(id+"F4.wireOp",EDGE,"E43.8.0.2")}),-1.0]])]});
            var Q14;
            Q14=makeQuery(id+"F4.imprint","IMPRINT",FACE,{"disambiguationData":[TD([[makeQuery(id+"F4.imprint","IMPRINT",EDGE,{"derivedFrom":sQuery(id+"F4.wireOp",EDGE,"E43.7.0.2")}),-1.0]])]});
            extrude(context, id + "F5", {"entities" : qUnion([Q0, Q1, Q2, Q3, Q4, Q5, Q6, Q7, Q8, Q9, Q10, Q11, Q12, Q13, Q14]), "operationType" : NewBodyOperationType.ADD, "depth" : 1 * mm});
        }
    });
